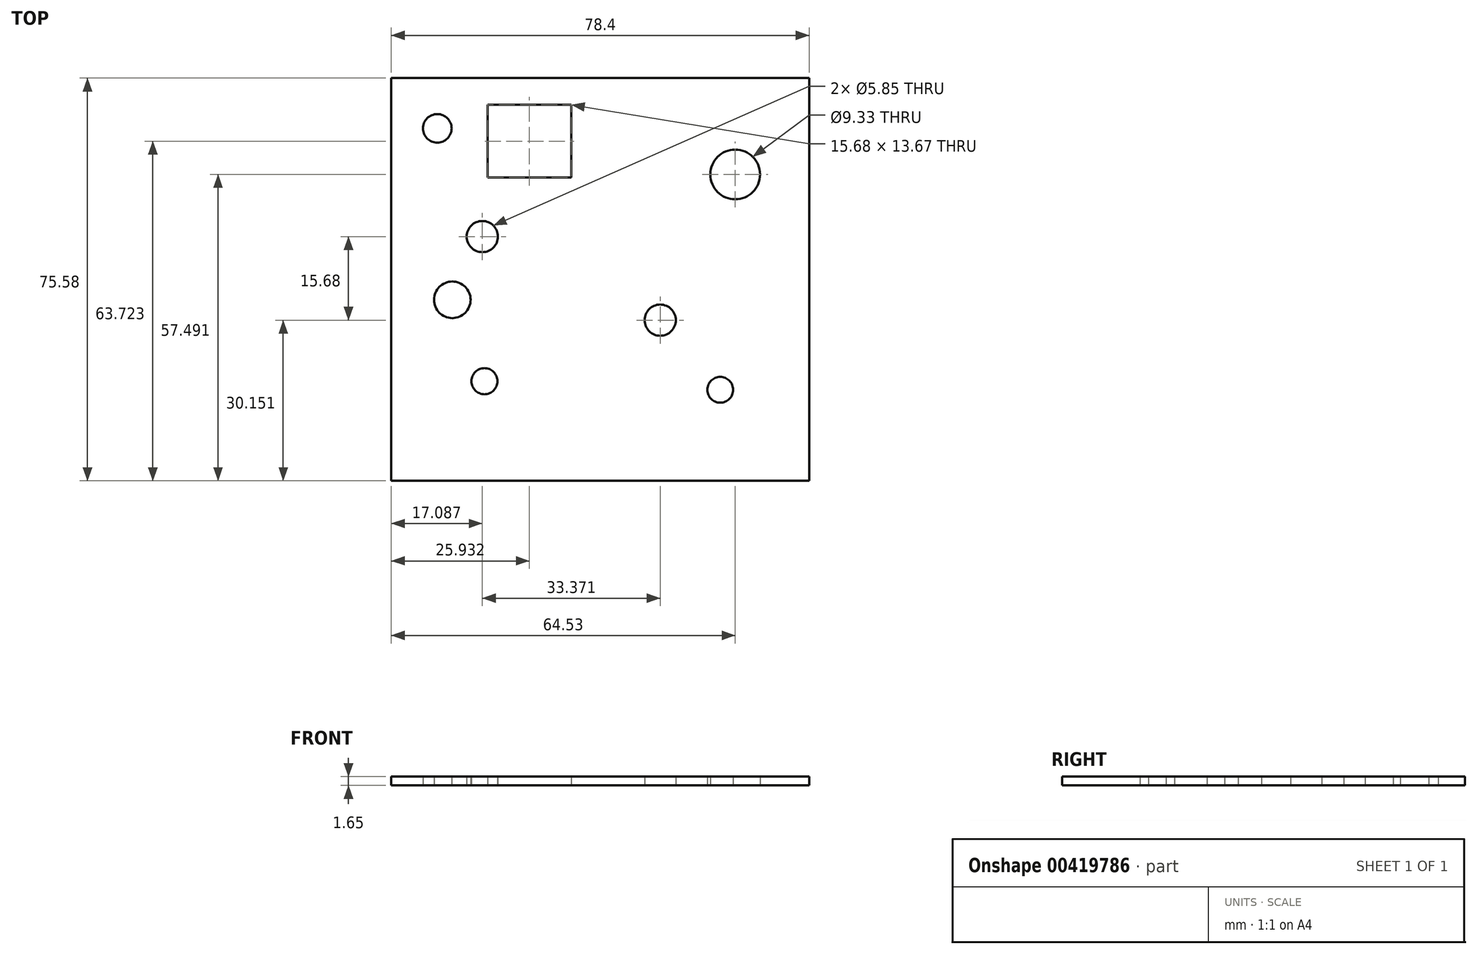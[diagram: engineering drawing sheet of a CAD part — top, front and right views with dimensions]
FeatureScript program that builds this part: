
annotation { "Feature Type Name" : "Feature", "Feature Type Description" : "" }
export const myFeature = defineFeature(function(context is Context, id is Id, definition is map)
    precondition{}
    {
        {
            var Q0;
            Q0=qCreatedBy(makeId("Top.planeOp"),FACE);
            var sketch = newSketch(context, id + "F0", { "sketchPlane" : qUnion([Q0])});
            skLineSegment(sketch, "E0.bottom", {"start": v(39.2, 37.8) * mm, "end": v(-39.2, 37.8) * mm});
            skLineSegment(sketch, "E0.top", {"start": v(39.2, -37.8) * mm, "end": v(-39.2, -37.8) * mm});
            skLineSegment(sketch, "E0.left", {"start": v(39.2, 37.8) * mm, "end": v(39.2, -37.8) * mm});
            skLineSegment(sketch, "E0.right", {"start": v(-39.2, 37.8) * mm, "end": v(-39.2, -37.8) * mm});
            skPoint(sketch, "E0.middle", {"position": v(0, 0) * mm});
            skCircle(sketch, "E1", {"center": v(-30.56, 28.35) * mm, "radius": 2.68 * mm});
            skCircle(sketch, "E2", {"center": v(25.33, 19.7) * mm, "radius": 4.66 * mm});
            skCircle(sketch, "E3", {"center": v(-21.71, -19.1) * mm, "radius": 2.45 * mm});
            skCircle(sketch, "E4", {"center": v(22.52, -20.7) * mm, "radius": 2.42 * mm});
            skCircle(sketch, "E5", {"center": v(11.26, -7.64) * mm, "radius": 2.93 * mm});
            skCircle(sketch, "E6", {"center": v(-27.74, -3.82) * mm, "radius": 3.44 * mm});
            skCircle(sketch, "E7", {"center": v(-22.11, 8.04) * mm, "radius": 2.93 * mm});
            skLineSegment(sketch, "E8.bottom", {"start": v(-5.43, 19.1) * mm, "end": v(-21.1, 19.1) * mm});
            skLineSegment(sketch, "E8.top", {"start": v(-5.43, 32.77) * mm, "end": v(-21.1, 32.77) * mm});
            skLineSegment(sketch, "E8.left", {"start": v(-5.43, 19.1) * mm, "end": v(-5.43, 32.77) * mm});
            skLineSegment(sketch, "E8.right", {"start": v(-21.1, 19.1) * mm, "end": v(-21.1, 32.77) * mm});
            skPoint(sketch, "E8.middle", {"position": v(-13.27, 25.93) * mm});
            skSolve(sketch);
        }
        {
            var Q0;
            Q0=qSketchRegion(id+"F0",true);
            extrude(context, id + "F1", {"entities" : qUnion([Q0]), "depth" : 1.65 * mm});
        }
    });
